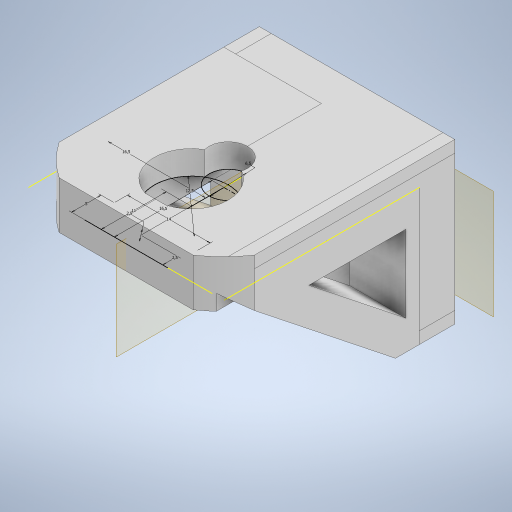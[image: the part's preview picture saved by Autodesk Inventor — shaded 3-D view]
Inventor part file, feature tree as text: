
AUTODESK INVENTOR PART (.ipt)
format: ipt  version: 2024 (Build 280153000, 153)  size: 847,360 bytes
history: native  units: mm
features: extrude x9, reference x6, projected_geometry x5, other x5, sketch x3, plane x2, mirror x1
ambient origin geometry x8: Origin, YZ Plane, XZ Plane, XY Plane, X Axis, Y Axis, Z Axis, Center Point
bodies: Solid1 (feature_tree)
feature tree (31):
  plane  "Work Plane1"
  extrude  "Extrusion1"  Depth=4.0mm
  extrude  "Extrusion7"  Depth=11.0mm
  extrude  "Extrusion9"  Depth=10.0mm
  extrude  "Extrusion8"  Depth=10.0mm
  extrude  "Extrusion10"  Depth=10.0mm
  extrude  "Extrusion11"  Depth=10.0mm
  plane  "Work Plane3"
  mirror  "Mirror3"
  extrude  "Extrusion12"  Depth=10.0mm
  extrude  "Extrusion13"  Depth=10.0mm
  extrude  "Extrusion15"  Depth=10.0mm
  reference  "Reference1"
  reference  "Reference2"
  reference  "Reference3"
  reference  "Reference4"
  reference  "Reference5"
  reference  "Reference6"
  projected_geometry  "Projected Loop4"
  projected_geometry  "Projected Loop5"
  sketch  "Sketch15"  dims[d0=6.0mm d1=0.0mm d42=4.0mm]
  projected_geometry  "Projected Loop6"
  sketch  "Sketch16"  dims[d43=33.0mm d44=0.0mm d46=11.0mm]
  projected_geometry  "Projected Loop7"
  projected_geometry  "Projected Loop8"
  sketch  "Sketch18"  dims[d47=12.5mm d48=6.5mm d49=14.0mm d50=5.0mm d51=2.5mm d52=16.5mm d53=2.5mm d54=16.5mm d55=4.0mm d56=0.0mm d57=0.0mm d58=0.0mm d59=3.0mm d60=3.0mm d61=20.0mm d62=0.0mm d65=4.0mm d66=0.0mm d67=-16.5mm d89=10.0mm d90=5.0mm d91=10.0mm d92=0.0mm d93=0.0mm d94=0.0mm d111=40.0mm d112=22.500017mm d113=10.0mm d114=0.0mm d30=0.5mm d31=0.872665mm d32=0.5mm d33=0.872665mm d95=0.5mm d96=0.872665mm d107=0.0mm d108=0.0mm d109=0.0mm d110=0.0mm]
  other  "<userpath> windows\Documents\Inventor\Robotska_roka\Assembly4.iam"
  other  "Assembly4.iam"
  other  "SG90 - Micro Servo 9g - Tower Pro:1"
  other  "SG90 - Micro Servo 9g - Tower Pro.4"
  other  "roka2:1"
